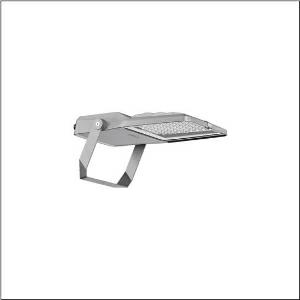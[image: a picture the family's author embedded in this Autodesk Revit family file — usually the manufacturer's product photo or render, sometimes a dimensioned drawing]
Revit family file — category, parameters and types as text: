
# Revit family: floodlight_fl_21_iq_mini___pl61_5xa7772b1c1a_06a2
name_source: partatom
category: Lighting Fixtures
units: mm (PartAtom-declared; Revit-internal decimal feet)

## family parameters
Cut with Voids When Loaded = No
Host = Face
Light Source = No
Part Type = Normal
Room Calculation Point = No
Round Connector Dimension = Use Diameter
Shared = No

## types (1)
- --- (1 x LED, 5080 lm, 45.5 W, 2200K)
    Apparent Load = 46 VA
    CIE Flux Codes = 33 65 98 100 100
    Color Rendering = 70
    Color Temperature = 2200K
    Default Elevation = 1800 mm
    Description = Floodlight FL 21 iQ mini, floodlight, primary light control with lens, of PMMA, primary optical cover: protective disc, of toughened safety glass, transparent, light distribution: PL61, light emission: direct distribution, installation type: surface-mounted, LED, High Power LED, rated luminous flux: 5.080lm, luminous efficacy: 112lm/W, light colour: 722, colour temperature: 2200K, control gear: iQ Street-Remote/DALI, control: Street-Remote, Auto-Match, Temp-Guard, Night-Set, Smart-Wire, Desk-Remote (wireless, voltage-free reading and setting of iQ features in the workshop via application-optimized NFC function/RFID function), optimised constant luminous flux control (CLO 2.0), with terminal, 6-pole, mains connection: 220..240V, AC, 50/60Hz, start of lifetime: 46W, end of service life: 48W, reduction: 21W, luminaire housing, of diecast aluminium, powder-coated, Siteco® metallic grey (DB 702S), corrosivity category C5 mid according to DIN EN ISO 12944, suitable for swimming pools, chlorine-resistant, sealing non-destructively replaceable, mounting bracket, of steel, galvanised, powder-coated, Siteco® metallic grey (DB 702S), protection rating (complete): IP66, insulation class (complete): insulation class II (safety insulation), certification: CE, ENEC, VDE, protection symbol: D, impact resistance: IK08, permissible operating ambient temperature: -40..+40°C, permissible operating ambient temperature for outdoor applications: -40..+50°C, standard: DIN EN 12944, LABS conformity tested according to VDMA 24364:2018-05, packaging unit: 1 piece

Light Distribution: PL61
    Height = 70 mm
    Lamp = 1 x LED
    Lamp Light Flux = 5080 lm
    Lamp Power = 45.5 W
    Lamp count = 1
    Length = 485 mm
    Luminous efficacy = 112 lm/W
    Manufacturer = Siteco
    ModVariant = No
    Model = 5XA7772B1C1A
    Number of Poles = 1
    OnlyDefault = Yes
    Power Factor = 1
    Product Name = Floodlight FL 21 iQ mini | PL61
    Product group = floodlight | pylon annexe
    ProductGroupID = 6200
    Protection Class = Protection class II
    Protection Degree = IP 66
    RLX_Detail_Level = 1
    RLX_Emergency_Light_Flux = 0 lm
    RLX_Emergency_Type = 0
    RLX_Emergency_Type_DB = No
    RlxData = <blob elided: 96229 chars, md5=24e5a1f8>
    Socket = socket
    Standby Power = 0 W
    System Light Flux = 5080 lm
    System Power = 46 W
    Type Comments = factory setting: luminous flux: 100 % | dim-lin: 254 | 463 mA
    Type Image = l_1006845.jpg
    URL = http://relux.com
    VarID = @adj_173692
    Voltage = 0 V
    Weight = 0.00 kg
    Width = 337 mm

## geometry (parser evidence)
native form markers: Blend x4, Sweep x11
no freeform markers — native parametric forms only
